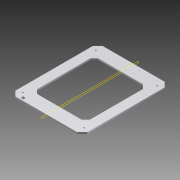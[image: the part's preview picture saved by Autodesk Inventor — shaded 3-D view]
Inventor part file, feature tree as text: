
AUTODESK INVENTOR PART (.ipt)
format: ipt  version: 2015 (Build 190159000, 159)  size: 199,680 bytes
history: native  units: mm
features: extrude x4, fillet x2, chamfer x2, projected_geometry x2, hole x1
ambient origin geometry x8: Origin, YZ Plane, XZ Plane, XY Plane, X Axis, Y Axis, Z Axis, Center Point
bodies: Solid1 (feature_tree)
feature tree (11):
  extrude  "Extrusión1"  Depth=359.0mm
  fillet  "Empalme1"  Radius=436.5mm
  chamfer  "Chaflán1"  Distance=65.0mm
  hole  "Agujero1"  [1 undecoded]
  extrude  "Extrusión4"  TaperAngle=45.0deg  [1 undecoded]
  fillet  "Empalme2"  Radius=20.0mm
  extrude  "Extrusión5"  Depth=25.0mm
  chamfer  "Chaflán3"  Distance=47.5mm
  extrude  "Extrusión3"  Depth=10.0mm
  projected_geometry  "Contorno proyectado1"
  projected_geometry  "Contorno proyectado2"
note: 2 required parameter values undecoded (feature->parameter linkage not recoverable at this tier; creation-order binding heuristic only, values carry confidence <= 0.55)
